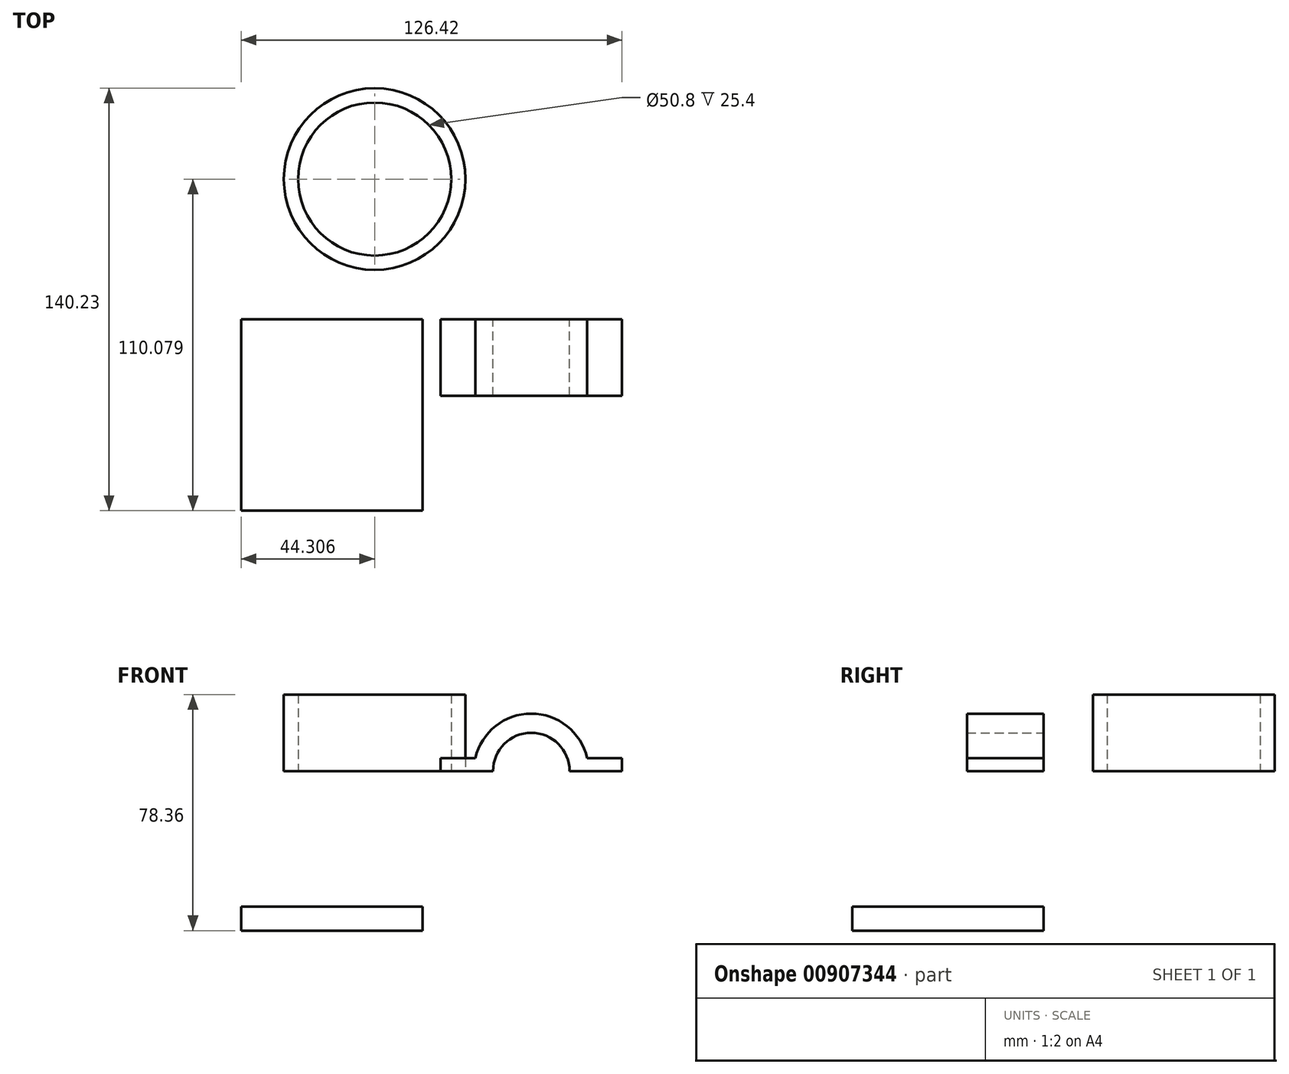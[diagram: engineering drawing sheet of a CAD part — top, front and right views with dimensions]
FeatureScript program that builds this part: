
annotation { "Feature Type Name" : "Feature", "Feature Type Description" : "" }
export const myFeature = defineFeature(function(context is Context, id is Id, definition is map)
    precondition{}
    {
        {
            var Q0;
            Q0=qCreatedBy(makeId("Front.planeOp"),FACE);
            var sketch = newSketch(context, id + "F0", { "sketchPlane" : qUnion([Q0])});
            skArc(sketch, "E0", {"start": v(12.7, 0) * mm, "mid": v(0, 12.7) * mm, "end": v(-12.7, 0) * mm});
            skLineSegment(sketch, "E1.bottom", {"start": v(30.12, 4.3) * mm, "end": v(18.56, 4.3) * mm});
            skLineSegment(sketch, "E1.left", {"start": v(30.12, 4.3) * mm, "end": v(30.12, 0) * mm});
            skLineSegment(sketch, "E1.right", {"start": v(-30.12, 4.3) * mm, "end": v(-30.12, 0) * mm});
            skLineSegment(sketch, "E2", {"start": v(-30.12, 0) * mm, "end": v(-12.7, 0) * mm});
            skLineSegment(sketch, "E3", {"start": v(30.12, 0) * mm, "end": v(12.7, 0) * mm});
            skArc(sketch, "E4.trimOffspring", {"start": v(18.56, 4.3) * mm, "mid": v(0, 19.05) * mm, "end": v(-18.56, 4.3) * mm});
            skLineSegment(sketch, "E5.trimOffspring", {"start": v(-18.56, 4.3) * mm, "end": v(-30.12, 4.3) * mm});
            skSolve(sketch);
        }
        {
            var Q0;
            Q0=makeQuery(id+"F0.imprint","IMPRINT",FACE,{"disambiguationData":[TD([[makeQuery(id+"F0.imprint","IMPRINT",EDGE,{"derivedFrom":sQuery(id+"F0.wireOp",EDGE,"E0")}),-1.0]])]});
            extrude(context, id + "F1", {"entities" : qUnion([Q0]), "depth" : 25.4 * mm, "offsetDistance" : 25.4 * mm});
        }
        {
            var Q0;
            Q0=qCreatedBy(makeId("Front.planeOp"),FACE);
            var sketch = newSketch(context, id + "F2", { "sketchPlane" : qUnion([Q0])});
            skLineSegment(sketch, "E6.bottom", {"start": v(-36.05, -44.96) * mm, "end": v(-96.3, -44.96) * mm});
            skLineSegment(sketch, "E6.top", {"start": v(-36.05, -52.96) * mm, "end": v(-96.3, -52.96) * mm});
            skLineSegment(sketch, "E6.left", {"start": v(-36.05, -44.96) * mm, "end": v(-36.05, -52.96) * mm});
            skLineSegment(sketch, "E6.right", {"start": v(-96.3, -44.96) * mm, "end": v(-96.3, -52.96) * mm});
            skPoint(sketch, "E6.middle", {"position": v(-66.17, -48.96) * mm});
            skSolve(sketch);
        }
        {
            var Q0;
            Q0=makeQuery(id+"F2.imprint","IMPRINT",FACE,{"disambiguationData":[TD([[makeQuery(id+"F2.imprint","IMPRINT",EDGE,{"derivedFrom":sQuery(id+"F2.wireOp",EDGE,"E6.bottom")}),1.0]])]});
            extrude(context, id + "F3", {"entities" : qUnion([Q0]), "depth" : 63.5 * mm, "offsetDistance" : 25.4 * mm});
        }
        {
            var Q0;
            Q0=qCreatedBy(makeId("Top.planeOp"),FACE);
            var sketch = newSketch(context, id + "F4", { "sketchPlane" : qUnion([Q0])});
            skCircle(sketch, "E7", {"center": v(-52, 46.58) * mm, "radius": 25.4 * mm});
            skCircle(sketch, "E8", {"center": v(-52, 46.58) * mm, "radius": 30.15 * mm});
            skSolve(sketch);
        }
        {
            var Q0;
            Q0=makeQuery(id+"F4.imprint","IMPRINT",FACE,{"disambiguationData":[TD([[makeQuery(id+"F4.imprint","IMPRINT",EDGE,{"derivedFrom":sQuery(id+"F4.wireOp",EDGE,"E7")}),-1.0]])]});
            extrude(context, id + "F5", {"entities" : qUnion([Q0]), "depth" : 25.4 * mm, "offsetDistance" : 25.4 * mm});
        }
    });
